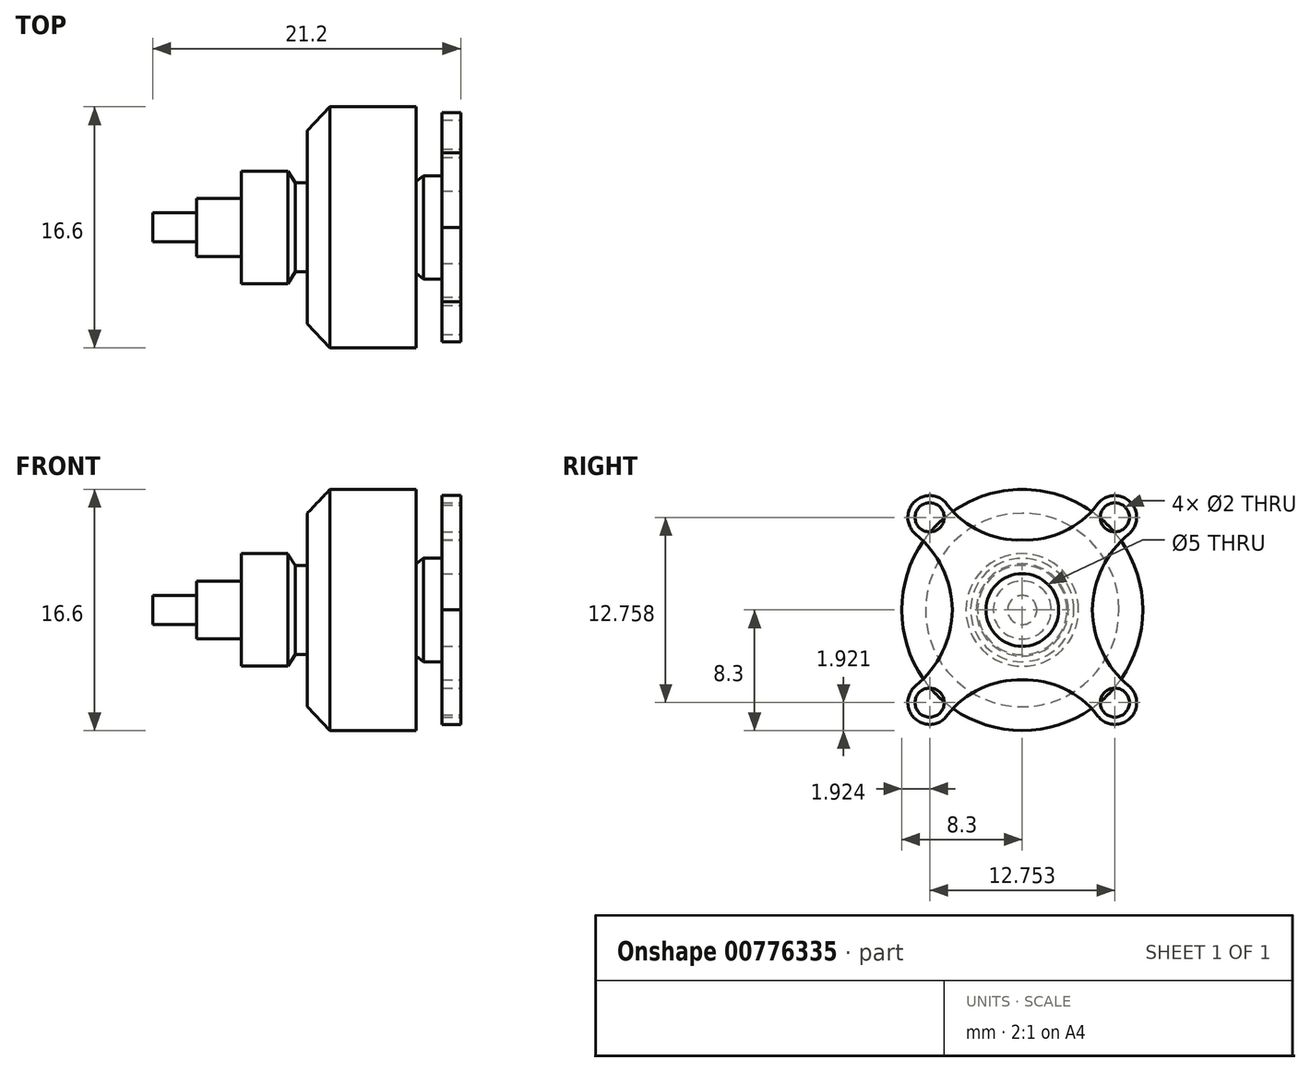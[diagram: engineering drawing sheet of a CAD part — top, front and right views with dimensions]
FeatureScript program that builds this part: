
annotation { "Feature Type Name" : "Feature", "Feature Type Description" : "" }
export const myFeature = defineFeature(function(context is Context, id is Id, definition is map)
    precondition{}
    {
        {
            var Q0;
            Q0=qCreatedBy(makeId("Right.planeOp"),FACE);
            var sketch = newSketch(context, id + "F0", { "sketchPlane" : qUnion([Q0])});
            skCircle(sketch, "E0", {"center": v(0, 0) * mm, "radius": 9 * mm, "construction": true});
            skCircle(sketch, "E1.1.0", {"center": v(6.38, 6.38) * mm, "radius": 1 * mm});
            skLineSegment(sketch, "E1.anchor1", {"start": v(0, 0) * mm, "end": v(0, 9) * mm, "construction": true});
            skLineSegment(sketch, "E1.anchor2", {"start": v(0, 0) * mm, "end": v(9, 0) * mm, "construction": true});
            skArc(sketch, "E2", {"start": v(7.33, 5.22) * mm, "mid": v(7.39, 7.49) * mm, "end": v(5.14, 7.23) * mm});
            skArc(sketch, "E3", {"start": v(0, 4.83) * mm, "mid": v(2.86, 5.4) * mm, "end": v(5.14, 7.23) * mm});
            skArc(sketch, "E4", {"start": v(7.33, 5.22) * mm, "mid": v(5.5, 2.89) * mm, "end": v(4.82, 0) * mm});
            skArc(sketch, "E5.MirrorCS", {"start": v(-7.33, 5.22) * mm, "mid": v(-5.5, 2.89) * mm, "end": v(-4.82, 0) * mm});
            skArc(sketch, "E6.MirrorCS", {"start": v(0, 4.83) * mm, "mid": v(-2.86, 5.4) * mm, "end": v(-5.14, 7.23) * mm});
            skCircle(sketch, "E7.MirrorC", {"center": v(-6.38, 6.38) * mm, "radius": 1 * mm});
            skArc(sketch, "E8.MirrorCS", {"start": v(-7.33, 5.22) * mm, "mid": v(-7.39, 7.49) * mm, "end": v(-5.14, 7.23) * mm});
            skLineSegment(sketch, "E9.MirrorCS", {"start": v(0, 0) * mm, "end": v(-9, 0) * mm, "construction": true});
            skArc(sketch, "E10.MirrorCS", {"start": v(0, -4.83) * mm, "mid": v(2.86, -5.4) * mm, "end": v(5.14, -7.23) * mm});
            skArc(sketch, "E11.MirrorCS", {"start": v(0, -4.83) * mm, "mid": v(-2.86, -5.4) * mm, "end": v(-5.14, -7.23) * mm});
            skCircle(sketch, "E12.MirrorC", {"center": v(-6.38, -6.38) * mm, "radius": 1 * mm});
            skArc(sketch, "E13.MirrorCS", {"start": v(7.33, -5.22) * mm, "mid": v(7.39, -7.49) * mm, "end": v(5.14, -7.23) * mm});
            skArc(sketch, "E14.MirrorCS", {"start": v(-7.33, -5.22) * mm, "mid": v(-7.39, -7.49) * mm, "end": v(-5.14, -7.23) * mm});
            skCircle(sketch, "E15.MirrorC", {"center": v(6.38, -6.38) * mm, "radius": 1 * mm});
            skArc(sketch, "E16.MirrorCS", {"start": v(-7.33, -5.22) * mm, "mid": v(-5.5, -2.89) * mm, "end": v(-4.82, 0) * mm});
            skArc(sketch, "E17.MirrorCS", {"start": v(7.33, -5.22) * mm, "mid": v(5.5, -2.89) * mm, "end": v(4.82, 0) * mm});
            skLineSegment(sketch, "E18.MirrorCS", {"start": v(0, 0) * mm, "end": v(0, -9) * mm, "construction": true});
            skCircle(sketch, "E19", {"center": v(0, 0) * mm, "radius": 2.5 * mm});
            skSolve(sketch);
        }
        {
            var Q0;
            Q0 = qSketchRegion(id + "F0", true);
            extrude(context, id + "F1", {"entities" : qUnion([Q0]), "oppositeDirection" : true, "depth" : 1.3 * mm, "offsetDistance" : 25 * mm});
        }
        {
            var Q0;
            Q0=qCreatedBy(makeId("Front.planeOp"),FACE);
            var sketch = newSketch(context, id + "F2", { "sketchPlane" : qUnion([Q0])});
            skLineSegment(sketch, "E20", {"start": v(-1.3, 3.56) * mm, "end": v(-2.57, 3.56) * mm});
            skLineSegment(sketch, "E21", {"start": v(-2.57, 3.56) * mm, "end": v(-3.08, 3.17) * mm});
            skLineSegment(sketch, "E22", {"start": v(-3.08, 3.17) * mm, "end": v(-3.08, 8.3) * mm});
            skLineSegment(sketch, "E23", {"start": v(-3.08, 8.3) * mm, "end": v(-9, 8.3) * mm});
            skLineSegment(sketch, "E24", {"start": v(-9, 8.3) * mm, "end": v(-10.55, 6.66) * mm});
            skLineSegment(sketch, "E25", {"start": v(-10.55, 6.66) * mm, "end": v(-10.55, 3.08) * mm});
            skLineSegment(sketch, "E26", {"start": v(-10.55, 3.08) * mm, "end": v(-11.4, 3.08) * mm});
            skLineSegment(sketch, "E27", {"start": v(-11.4, 3.08) * mm, "end": v(-11.91, 3.87) * mm});
            skLineSegment(sketch, "E28", {"start": v(-11.91, 3.87) * mm, "end": v(-15.1, 3.87) * mm});
            skLineSegment(sketch, "E29", {"start": v(-15.1, 3.87) * mm, "end": v(-15.1, 2) * mm});
            skLineSegment(sketch, "E30", {"start": v(-15.1, 2) * mm, "end": v(-18.2, 2) * mm});
            skLineSegment(sketch, "E31", {"start": v(-18.2, 2) * mm, "end": v(-18.2, 1) * mm});
            skLineSegment(sketch, "E32", {"start": v(-18.2, 1) * mm, "end": v(-21.2, 1) * mm});
            skLineSegment(sketch, "E33", {"start": v(-21.2, 1) * mm, "end": v(-21.2, 0) * mm});
            skLineSegment(sketch, "E34", {"start": v(0, 0) * mm, "end": v(-23.12, 0) * mm, "construction": true});
            skLineSegment(sketch, "E35", {"start": v(-1.3, 3.56) * mm, "end": v(-1.3, 0) * mm});
            skLineSegment(sketch, "E36", {"start": v(-21.2, 0) * mm, "end": v(-1.3, 0) * mm});
            skSolve(sketch);
        }
        {
            var Q0;
            Q0 = qSketchRegion(id + "F2", true);
            var Q1;
            Q1=sQuery(id+"F2.wireOp",EDGE,"E36");
            revolve(context, id + "F3", {"surfaceOperationType" : NewSurfaceOperationType.NEW, "entities" : qUnion([Q0]), "axis" : qUnion([Q1]), "revolveType" : RevolveType.FULL});
        }
    });
